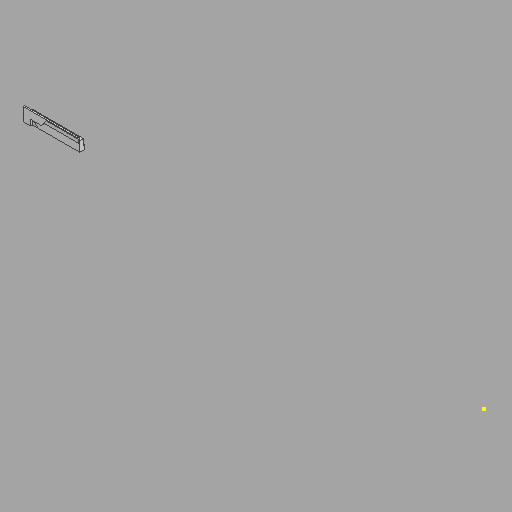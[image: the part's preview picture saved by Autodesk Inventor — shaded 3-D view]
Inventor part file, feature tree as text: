
AUTODESK INVENTOR PART (.ipt)
format: ipt  version: 2023 (Build 270158030, 158C)  size: 122,880 bytes
history: native  units: in
note: dims shown in document units (in); Inventor stores cm internally (conversion verified against a paired STEP export)
features: sketch x2, extrude x1, other x1
ambient origin geometry x8: Origin, YZ Plane, XZ Plane, XY Plane, X Axis, Y Axis, Z Axis, Center Point
bodies: Solid1 (feature_tree)
feature tree (4):
  sketch  "Sketch1"  dims[d0=1.0in d1=0.0in]
  extrude  "Extrusion1"  [1 undecoded]
  sketch  "Sketch2"
  other  "Screen sill I - 1"
note: 1 required parameter value undecoded (feature->parameter linkage not recoverable at this tier; creation-order binding heuristic only, values carry confidence <= 0.55)
